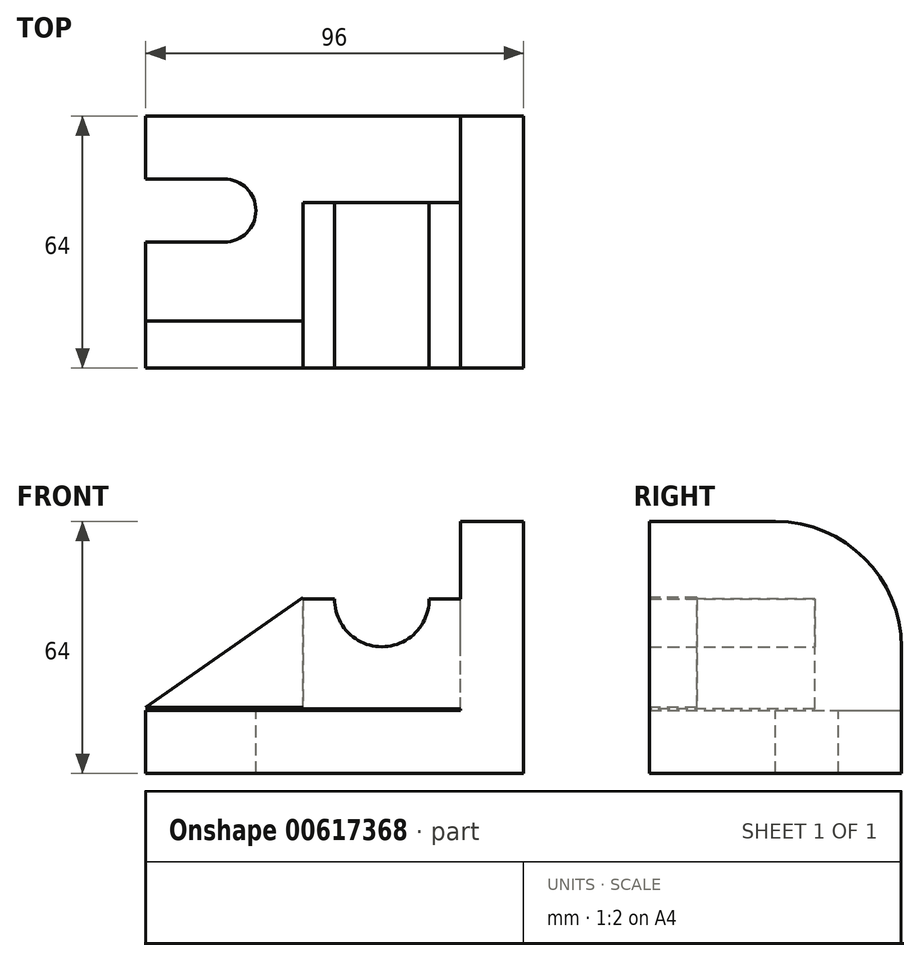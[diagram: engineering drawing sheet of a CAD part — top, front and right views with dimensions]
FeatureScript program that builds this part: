
annotation { "Feature Type Name" : "Feature", "Feature Type Description" : "" }
export const myFeature = defineFeature(function(context is Context, id is Id, definition is map)
    precondition{}
    {
        {
            var Q0;
            Q0=qCreatedBy(makeId("Top.planeOp"),FACE);
            var sketch = newSketch(context, id + "F0", { "sketchPlane" : qUnion([Q0])});
            skLineSegment(sketch, "E0.bottom", {"start": v(0, 0) * mm, "end": v(-80, 0) * mm});
            skLineSegment(sketch, "E0.top", {"start": v(0, 64) * mm, "end": v(-80, 64) * mm});
            skLineSegment(sketch, "E0.left", {"start": v(0, 0) * mm, "end": v(0, 64) * mm});
            skLineSegment(sketch, "E0.right", {"start": v(-80, 0) * mm, "end": v(-80, 64) * mm});
            skSolve(sketch);
        }
        {
            var Q0;
            Q0=makeQuery(id+"F0.imprint","IMPRINT",FACE,{"disambiguationData":[TD([[makeQuery(id+"F0.imprint","IMPRINT",EDGE,{"derivedFrom":sQuery(id+"F0.wireOp",EDGE,"E0.bottom")}),-1.0]])]});
            extrude(context, id + "F1", {"entities" : qUnion([Q0]), "depth" : 16 * mm, "offsetDistance" : 25.4 * mm});
        }
        {
            var Q0;
            Q0=qCreatedBy(makeId("Right.planeOp"),FACE);
            var sketch = newSketch(context, id + "F2", { "sketchPlane" : qUnion([Q0])});
            skLineSegment(sketch, "E1.bottom", {"start": v(11.74, -19.39) * mm, "end": v(12.25, -19.39) * mm});
            skLineSegment(sketch, "E1.top", {"start": v(11.74, -22.89) * mm, "end": v(12.25, -22.89) * mm});
            skLineSegment(sketch, "E1.left", {"start": v(11.74, -19.39) * mm, "end": v(11.74, -22.89) * mm});
            skLineSegment(sketch, "E1.right", {"start": v(12.25, -19.39) * mm, "end": v(12.25, -22.89) * mm});
            skLineSegment(sketch, "E2.bottom", {"start": v(0, 0) * mm, "end": v(64, 0) * mm});
            skLineSegment(sketch, "E2.top", {"start": v(0, 64) * mm, "end": v(64, 64) * mm});
            skLineSegment(sketch, "E2.left", {"start": v(0, 0) * mm, "end": v(0, 64) * mm});
            skLineSegment(sketch, "E2.right", {"start": v(64, 0) * mm, "end": v(64, 64) * mm});
            skSolve(sketch);
        }
        {
            var Q0;
            Q0=makeQuery(id+"F2.imprint","IMPRINT",FACE,{"disambiguationData":[TD([[makeQuery(id+"F2.imprint","IMPRINT",EDGE,{"derivedFrom":sQuery(id+"F2.wireOp",EDGE,"E2.bottom")}),1.0]])]});
            extrude(context, id + "F3", {"entities" : qUnion([Q0]), "operationType" : NewBodyOperationType.ADD, "depth" : 16 * mm, "offsetDistance" : 25.4 * mm});
        }
        {
            var Q0;
            Q0=makeQuery(id+"F3.opExtrude","SWEPT_EDGE",EDGE,{"disambiguationData":[OSD([sQuery(id+"F2.wireOp",EDGE,"E2.top"),sQuery(id+"F2.wireOp",EDGE,"E2.right")])]});
            fillet(context, id + "F4", {"entities" : qUnion([Q0]), "radius" : 32 * mm, "tangentPropagation" : true, "allowEdgeOverflow" : false});
        }
        {
            var Q0;
            Q0=qCreatedBy(makeId("Front.planeOp"),FACE);
            var sketch = newSketch(context, id + "F5", { "sketchPlane" : qUnion([Q0])});
            skLineSegment(sketch, "E3.0", {"start": v(0, 16) * mm, "end": v(0, 64) * mm});
            skLineSegment(sketch, "E4.bottom", {"start": v(-40, 16.37) * mm, "end": v(0, 16.37) * mm});
            skLineSegment(sketch, "E4.top", {"start": v(-40, 44.37) * mm, "end": v(0, 44.37) * mm});
            skLineSegment(sketch, "E4.left", {"start": v(-40, 16.37) * mm, "end": v(-40, 44.37) * mm});
            skLineSegment(sketch, "E4.right", {"start": v(0, 16.37) * mm, "end": v(0, 44.37) * mm});
            skPoint(sketch, "E4.middle", {"position": v(-20, 30.37) * mm});
            skSolve(sketch);
        }
        {
            var Q0;
            Q0=makeQuery(id+"F5.imprint","IMPRINT",FACE,{"disambiguationData":[TD([[makeQuery(id+"F5.imprint","IMPRINT",EDGE,{"derivedFrom":sQuery(id+"F5.wireOp",EDGE,"E4.bottom")}),1.0]])]});
            extrude(context, id + "F6", {"entities" : qUnion([Q0]), "operationType" : NewBodyOperationType.ADD, "oppositeDirection" : true, "depth" : 42 * mm, "offsetDistance" : 25.4 * mm});
        }
        {
            var Q0;
            Q0=makeQuery(id+"F6.opExtrude","CAP_FACE",FACE,{"disambiguationData":[OSD([sQuery(id+"F5.wireOp",EDGE,"E4.bottom"),sQuery(id+"F5.wireOp",EDGE,"E4.top"),sQuery(id+"F5.wireOp",EDGE,"E4.left"),sQuery(id+"F5.wireOp",EDGE,"E4.right")])],"isStart":false});
            var sketch = newSketch(context, id + "F7", { "sketchPlane" : qUnion([Q0])});
            skArc(sketch, "E5", {"start": v(8, 44.37) * mm, "mid": v(20, 32.18) * mm, "end": v(32, 44.37) * mm});
            skSolve(sketch);
        }
        {
            var Q0;
            {var subQ0=sQuery(id+"F7.wireOp",EDGE,"E5");Q0=makeQuery(id+"F7.imprint","IMPRINT",FACE,{"disambiguationData":[TD([[makeQuery(id+"F7.imprint","IMPRINT",EDGE,{"derivedFrom":subQ0}),1.0]])]});}
            extrude(context, id + "F8", {"entities" : qUnion([Q0]), "operationType" : NewBodyOperationType.REMOVE, "oppositeDirection" : true, "depth" : 42 * mm, "offsetDistance" : 25.4 * mm});
        }
        {
            var Q0;
            Q0=qCreatedBy(makeId("Front.planeOp"),FACE);
            var sketch = newSketch(context, id + "F9", { "sketchPlane" : qUnion([Q0])});
            skLineSegment(sketch, "E6", {"start": v(-40, 44.75) * mm, "end": v(-40, 16.75) * mm});
            skLineSegment(sketch, "E7", {"start": v(-40, 16.75) * mm, "end": v(-80, 16.75) * mm});
            skLineSegment(sketch, "E8", {"start": v(-80, 16.75) * mm, "end": v(-40, 44.75) * mm});
            skSolve(sketch);
        }
        {
            var Q0;
            Q0 = qSketchRegion(id + "F9", true);
            extrude(context, id + "F10", {"entities" : qUnion([Q0]), "operationType" : NewBodyOperationType.ADD, "oppositeDirection" : true, "depth" : 12 * mm, "offsetDistance" : 25.4 * mm});
        }
        {
            var Q0;
            Q0=makeQuery(id+"F1.opExtrude","CAP_FACE",FACE,{"disambiguationData":[OSD([sQuery(id+"F0.wireOp",EDGE,"E0.bottom"),sQuery(id+"F0.wireOp",EDGE,"E0.top"),sQuery(id+"F0.wireOp",EDGE,"E0.left"),sQuery(id+"F0.wireOp",EDGE,"E0.right")])],"isStart":false});
            var sketch = newSketch(context, id + "F11", { "sketchPlane" : qUnion([Q0])});
            skLineSegment(sketch, "E9", {"start": v(-80, 32) * mm, "end": v(-60, 32) * mm});
            skLineSegment(sketch, "E10", {"start": v(-60, 32) * mm, "end": v(-60, 48) * mm});
            skLineSegment(sketch, "E11", {"start": v(-60, 48) * mm, "end": v(-80, 48) * mm});
            skLineSegment(sketch, "E12", {"start": v(-80, 48) * mm, "end": v(-80, 32) * mm});
            skArc(sketch, "E13", {"start": v(-60, 32) * mm, "mid": v(-52, 40) * mm, "end": v(-60, 48) * mm});
            skSolve(sketch);
        }
        {
            var Q0;
            Q0 = qSketchRegion(id + "F11", true);
            extrude(context, id + "F12", {"entities" : qUnion([Q0]), "operationType" : NewBodyOperationType.REMOVE, "oppositeDirection" : true, "depth" : 16 * mm, "offsetDistance" : 25.4 * mm});
        }
    });
